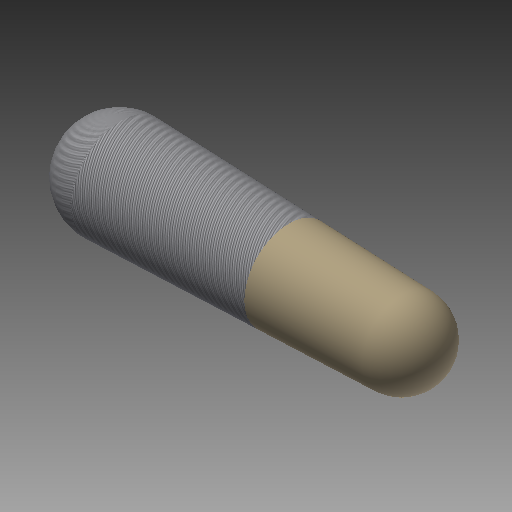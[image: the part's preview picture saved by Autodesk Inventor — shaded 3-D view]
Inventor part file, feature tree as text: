
AUTODESK INVENTOR PART (.ipt)
format: ipt  version: 2022 (Build 260153000, 153)  size: 228,352 bytes
history: native  units: mm (DEFAULTED — no unit token found)
features: other x1, revolve x1, plane x1, split x1, sketch x1
ambient origin geometry x8: Origin, YZ Plane, XZ Plane, XY Plane, X Axis, Y Axis, Z Axis, Center Point
bodies: Solid1 (feature_tree)
feature tree (5):
  other  "iMandy - 2D BODY"
  revolve  "Revolution1"  [1 undecoded]
  plane  "Work Plane1"
  split  "Split1"
  sketch  "Sketch1"  dims[d1=10.0mm d16=261.62mm d17=92.456mm d18=75.692mm d19=90.0deg d20=-156.972mm]
note: 1 required parameter value undecoded (feature->parameter linkage not recoverable at this tier; creation-order binding heuristic only, values carry confidence <= 0.55)
